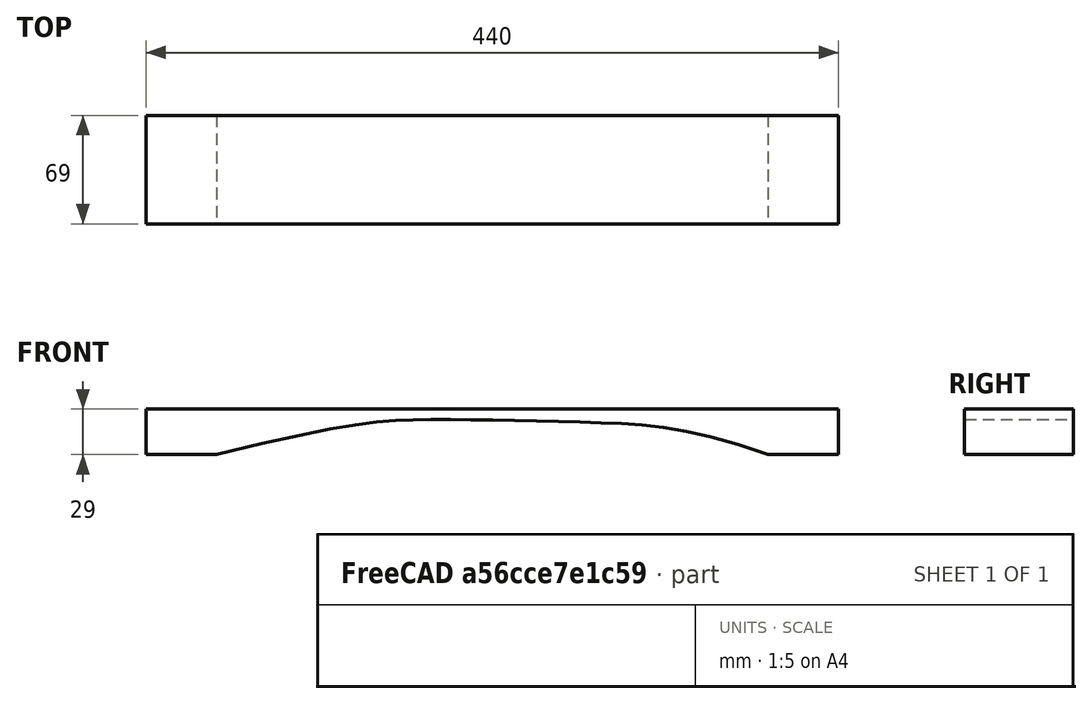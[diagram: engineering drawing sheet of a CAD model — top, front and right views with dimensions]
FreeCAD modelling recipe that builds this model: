
FCSTD DOCUMENT  (FreeCAD 0.20R29410 (Git))
Label: Single_Bar2
License: All rights reserved
LicenseURL: http://en.wikipedia.org/wiki/All_rights_reserved
objects: Sketcher::SketchObject×1, Part::Extrusion×1, Fem::FemSolverObjectPython×1, App::MaterialObjectPython×1, Fem::ConstraintDisplacement×1, Fem::FemMeshShapeNetgenObject×1, Fem::FemAnalysis×1
note: 2 computed .brp shape members not serialized (recipe doc carries the construction recipe); baked Part::Feature solids carry a one-line shape summary decoded from their .brp

FEATURE [Sketcher::SketchObject] Sketch
  FullyConstrained = true
  Placement = pos=(0,0,0) rot=(1,0,0;1.5708rad)
  sketch-geometry (12):
    g0: LineSegment StartX=44.78 StartY=0 StartZ=0 EndX=0 EndY=0 EndZ=0
    g1: LineSegment StartX=0 StartY=0 StartZ=0 EndX=0 EndY=29 EndZ=0
    g2: LineSegment StartX=0 StartY=29 StartZ=0 EndX=440 EndY=29 EndZ=0
    g3: LineSegment StartX=440 StartY=29 StartZ=0 EndX=440 EndY=0 EndZ=0
    g4: LineSegment StartX=440 StartY=0 StartZ=0 EndX=395.22 EndY=0 EndZ=0
    g5-g10: Circle x6 (B-spline internal-alignment scaffolding for g11; pole/knot coordinates omitted)
    g11: BSplineCurve PolesCount=6 KnotsCount=4 Degree=3 IsPeriodic=0
  constraints (38):
    c: DistanceX(g0) = 0
    c: DistanceY(g0) = 0
    c: Distance(g1,g1) = 29
    c: Distance(g2,g2) = 440
    c: DistanceX(g0,g0) = 44.78
    c: DistanceX(g4,g4) = 44.78
    c: Horizontal(g0)
    c: Vertical(g1)
    c: Horizontal(g2)
    c: Vertical(g3)
    c: Horizontal(g4)
    c: Equal(g3,g1)
    c: Coincident(g0,g1)
    c: Coincident(g1,g2)
    c: Coincident(g2,g3)
    c: Coincident(g3,g4)
    c: DistanceX(g6) = 343.71
    c: DistanceY(g6) = 18.63
    c: DistanceX(g7) = 284.82
    c: DistanceY(g7) = 20.42
    c: DistanceX(g8) = 168.2
    c: DistanceY(g8) = 23.47
    c: DistanceX(g9) = 126.8
    c: DistanceY(g9) = 20.13
    c: Weight(g5) = 1
    c: InternalAlignment(g5,g11)
    c: Weight(g6) = 1
    c: InternalAlignment(g6,g11)
    c: Weight(g7) = 1
    c: InternalAlignment(g7,g11)
    c: Weight(g8) = 1
    c: InternalAlignment(g8,g11)
    c: Weight(g9) = 1
    c: InternalAlignment(g9,g11)
    c: Weight(g10) = 1
    c: InternalAlignment(g10,g11)
    c: Coincident(g4,g11)
    c: Coincident(g0,g11)
FEATURE [Part::Extrusion] Bar
  Base = -> Sketch
  Dir = (0,-1,-3e-16)
  DirMode = 2
  FaceMakerClass = Part::FaceMakerBullseye
  LengthFwd = 69
  LengthRev = 0
  Solid = true
  Symmetric = false
FEATURE [Fem::FemSolverObjectPython] SolverCcxTools  # FEM object (typed FeaturePython)
  AnalysisType = 0
  BeamShellResultOutput3D = false
  BucklingFactors = 1
  EigenmodeHighLimit = 20000
  EigenmodeLowLimit = 20
  EigenmodesCount = 12
  GeometricalNonlinearity = 0
  IterationsControlParameterCutb = 0.25,0.5,0.75,0.85,,,1.5,
  IterationsControlParameterIter = 4,8,9,200,10,400,,200,,
  IterationsControlParameterTimeUse = false
  IterationsThermoMechMaximum = 2000
  IterationsUserDefinedIncrementations = false
  IterationsUserDefinedTimeStepLength = false
  MaterialNonlinearity = 0
  MatrixSolverType = 0
  SplitInputWriter = false
  ThermoMechSteadyState = false
  TimeEnd = 1
  TimeInitialStep = 0.01
FEATURE [App::MaterialObjectPython] MaterialSolid  # material (typed FeaturePython)
  Category = 0
  Material = CompressiveStrength=7800 kPa,Density=670 kg/m^3,Name=White European Oak,PoissonRatio=0.37,ShearModulus=11.6 MPa,UltimateTensileStrength=97.1 MPa,+1 more (map truncated)
FEATURE [Fem::ConstraintDisplacement] FemConstraintDisplacement
  NormalDirection = (0,3e-16,-1)
  Normals = (116) [(0,3.33067e-16,-1),(0,3.33067e-16,-1),(0,3.33067e-16,-1),(0,3.33067e-16,-1),(0,3.33067e-16,-1),(0,3.33067e-16,-1),(0,3.33067e-16,-1),+109 more]
  Points = (116) [(44.78,-69,-2.29816e-14),(29.8533,-69,-2.29816e-14),(14.9267,-69,-2.29816e-14),(0,-69,-2.29816e-14),(44.78,-46,-1.53211e-14),+111 more]
  References = -> [Bar]
  rotxFix = false
  rotxFree = true
  rotyFix = false
  rotyFree = true
  rotzFix = false
  rotzFree = true
  xDisplacement = 0
  xFix = false
  xFree = true
  xRotation = 0
  yDisplacement = 0
  yFix = true
  yFree = false
  yRotation = 0
  zDisplacement = 0
  zFix = false
  zFree = true
  zRotation = 0
FEATURE [Fem::FemMeshShapeNetgenObject] FEMMeshNetgen
  Fineness = 4
  GrowthRate = 0.3
  MaxSize = 10
  NbSegsPerEdge = 1
  NbSegsPerRadius = 2
  Optimize = true
  SecondOrder = true
  Shape = -> Bar
FEATURE [Fem::FemAnalysis] Analysis
  Group = -> [SolverCcxTools,MaterialSolid,FemConstraintDisplacement,FEMMeshNetgen]
